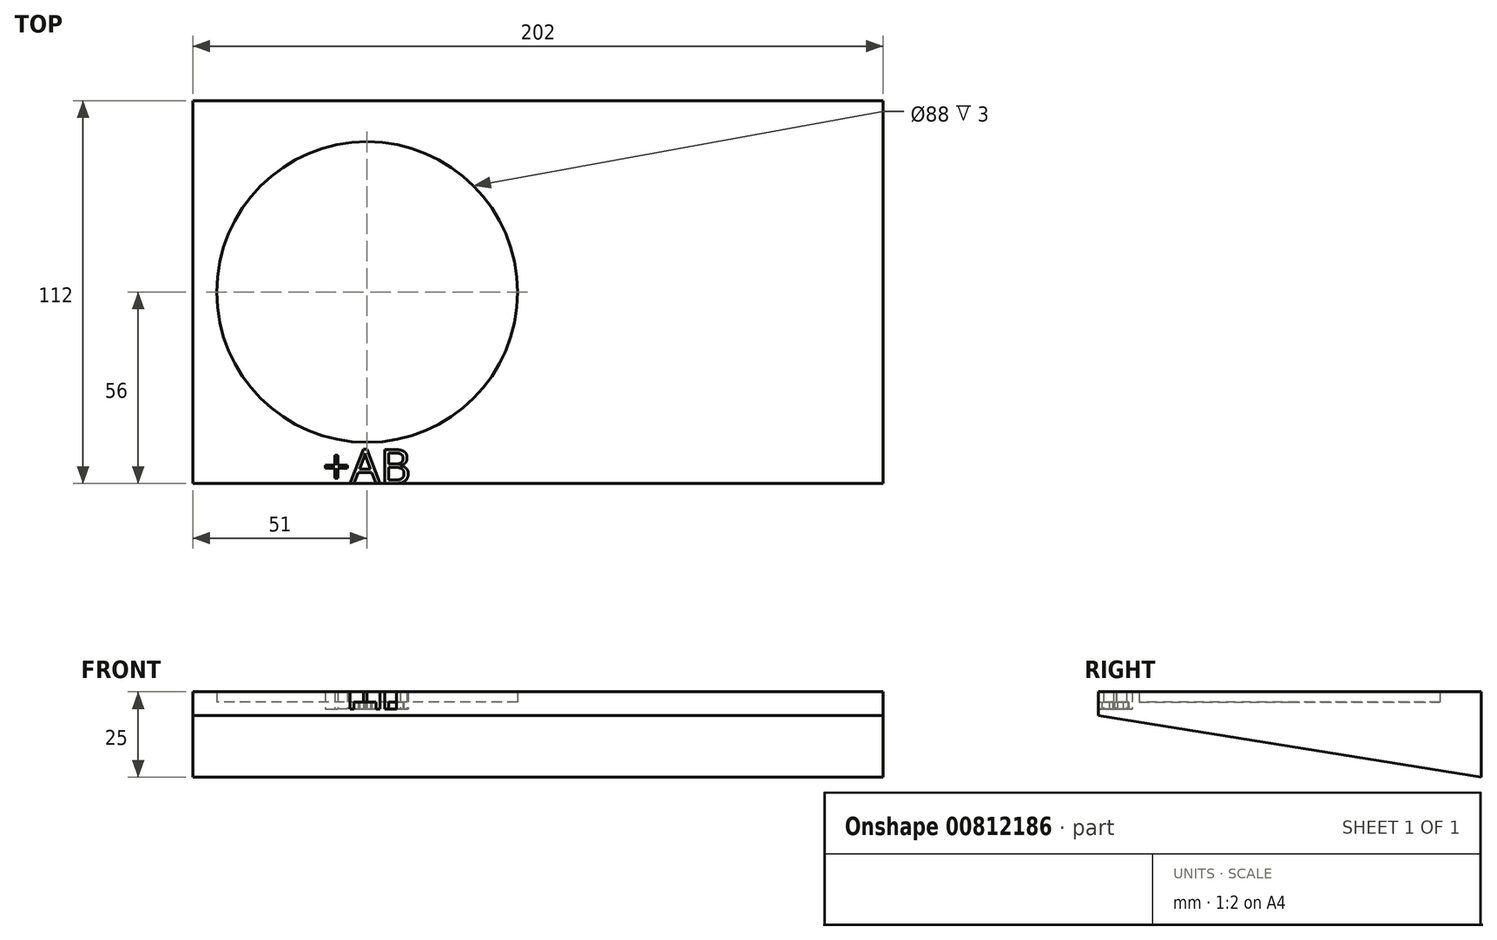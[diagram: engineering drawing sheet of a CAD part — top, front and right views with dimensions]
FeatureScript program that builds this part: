
annotation { "Feature Type Name" : "Feature", "Feature Type Description" : "" }
export const myFeature = defineFeature(function(context is Context, id is Id, definition is map)
    precondition{}
    {
        {
            var Q0;
            Q0=qCreatedBy(makeId("Top.planeOp"),FACE);
            var sketch = newSketch(context, id + "F0", { "sketchPlane" : qUnion([Q0])});
            skCircle(sketch, "E0", {"center": v(-50, 0) * mm, "radius": 46 * mm});
            skCircle(sketch, "E1", {"center": v(-50, 0) * mm, "radius": 44 * mm});
            skCircle(sketch, "E2.MirrorC", {"center": v(50, 0) * mm, "radius": 44 * mm});
            skCircle(sketch, "E3.MirrorC", {"center": v(50, 0) * mm, "radius": 46 * mm});
            skLineSegment(sketch, "E4.bottom", {"start": v(101, -56) * mm, "end": v(-101, -56) * mm});
            skLineSegment(sketch, "E4.top", {"start": v(101, 56) * mm, "end": v(-101, 56) * mm});
            skLineSegment(sketch, "E4.left", {"start": v(101, -56) * mm, "end": v(101, 56) * mm});
            skLineSegment(sketch, "E4.right", {"start": v(-101, -56) * mm, "end": v(-101, 56) * mm});
            skPoint(sketch, "E4.middle", {"position": v(0, 0) * mm});
            skText(sketch, "E5", { "text": "+AB", "fontName": "OpenSans-Regular.ttf"});
            skLineSegment(sketch, "E6", {"start": v(-50, 56) * mm, "end": v(-50, -56) * mm, "construction": true});
            skLineSegment(sketch, "E7", {"start": v(50, 56) * mm, "end": v(50, -56) * mm, "construction": true});
            const initialGuessF0  = {"E5": [-0.06293, -0.056, 1, 0, 0.01]};
            skSetInitialGuess(sketch, initialGuessF0);
            skSolve(sketch);
        }
        {
            var Q0;
            Q0=makeQuery(id+"F0.imprint","IMPRINT",FACE,{"disambiguationData":[TD([[makeQuery(id+"F0.imprint","IMPRINT",EDGE,{"derivedFrom":sQuery(id+"F0.wireOp",EDGE,"E0")}),-1.0]])]});
            var Q1;
            Q1=makeQuery(id+"F0.imprint","IMPRINT",FACE,{"disambiguationData":[TD([[makeQuery(id+"F0.imprint","IMPRINT",EDGE,{"derivedFrom":sQuery(id+"F0.wireOp",EDGE,"E0")}),1.0]])]});
            var Q2;
            Q2=makeQuery(id+"F0.imprint","IMPRINT",FACE,{"disambiguationData":[TD([[makeQuery(id+"F0.imprint","IMPRINT",EDGE,{"derivedFrom":sQuery(id+"F0.wireOp",EDGE,"E1")}),1.0]])]});
            var Q3;
            Q3=makeQuery(id+"F0.imprint","IMPRINT",FACE,{"disambiguationData":[TD([[makeQuery(id+"F0.imprint","IMPRINT",EDGE,{"derivedFrom":sQuery(id+"F0.wireOp",EDGE,"E2.MirrorC")}),-1.0]])]});
            var Q4;
            Q4=makeQuery(id+"F0.imprint","IMPRINT",FACE,{"disambiguationData":[TD([[makeQuery(id+"F0.imprint","IMPRINT",EDGE,{"derivedFrom":sQuery(id+"F0.wireOp",EDGE,"E2.MirrorC")}),1.0]])]});
            var Q5;
            Q5=makeQuery(id+"F0.imprint","IMPRINT",FACE,{"disambiguationData":[TD([[makeQuery(id+"F0.imprint","IMPRINT",EDGE,{"derivedFrom":sQuery(id+"F0.wireOp",EDGE,"E5.sketch_text.stroke-20")}),1.0]])]});
            var Q6;
            {var subQ0=sQuery(id+"F0.wireOp",EDGE,"E5.sketch_text.stroke-12");Q6=makeQuery(id+"F0.imprint","IMPRINT",FACE,{"disambiguationData":[TD([[makeQuery(id+"F0.imprint","IMPRINT",EDGE,{"derivedFrom":subQ0}),1.0]])]});}
            var Q7;
            Q7=makeQuery(id+"F0.imprint","IMPRINT",FACE,{"disambiguationData":[TD([[makeQuery(id+"F0.imprint","IMPRINT",EDGE,{"derivedFrom":sQuery(id+"F0.wireOp",EDGE,"E5.sketch_text.stroke-36")}),1.0]])]});
            var Q8;
            Q8=makeQuery(id+"F0.imprint","IMPRINT",FACE,{"disambiguationData":[TD([[makeQuery(id+"F0.imprint","IMPRINT",EDGE,{"derivedFrom":sQuery(id+"F0.wireOp",EDGE,"E5.sketch_text.stroke-43")}),1.0]])]});
            extrude(context, id + "F1", {"entities" : qUnion([Q0, Q1, Q2, Q3, Q4, Q5, Q6, Q7, Q8]), "depth" : 2 * mm, "offsetDistance" : 25 * mm});
        }
        {
            var Q0;
            Q0=makeQuery(id+"F1.opExtrude","CAP_FACE",FACE,{"disambiguationData":[OSD([sQuery(id+"F0.wireOp",EDGE,"E4.bottom"),sQuery(id+"F0.wireOp",EDGE,"E4.top"),sQuery(id+"F0.wireOp",EDGE,"E4.left"),sQuery(id+"F0.wireOp",EDGE,"E4.right"),sQuery(id+"F0.wireOp",EDGE,"E5.sketch_text.stroke-0"),sQuery(id+"F0.wireOp",EDGE,"E5.sketch_text.stroke-1"),sQuery(id+"F0.wireOp",EDGE,"E5.sketch_text.stroke-2"),sQuery(id+"F0.wireOp",EDGE,"E5.sketch_text.stroke-3"),sQuery(id+"F0.wireOp",EDGE,"E5.sketch_text.stroke-4"),sQuery(id+"F0.wireOp",EDGE,"E5.sketch_text.stroke-5"),sQuery(id+"F0.wireOp",EDGE,"E5.sketch_text.stroke-6"),sQuery(id+"F0.wireOp",EDGE,"E5.sketch_text.stroke-7"),sQuery(id+"F0.wireOp",EDGE,"E5.sketch_text.stroke-8"),sQuery(id+"F0.wireOp",EDGE,"E5.sketch_text.stroke-9"),sQuery(id+"F0.wireOp",EDGE,"E5.sketch_text.stroke-10"),sQuery(id+"F0.wireOp",EDGE,"E5.sketch_text.stroke-11"),sQuery(id+"F0.wireOp",EDGE,"E5.sketch_text.stroke-16"),sQuery(id+"F0.wireOp",EDGE,"E5.sketch_text.stroke-17"),sQuery(id+"F0.wireOp",EDGE,"E5.sketch_text.stroke-18"),sQuery(id+"F0.wireOp",EDGE,"E5.sketch_text.stroke-25"),sQuery(id+"F0.wireOp",EDGE,"E5.sketch_text.stroke-26"),sQuery(id+"F0.wireOp",EDGE,"E5.sketch_text.stroke-27"),sQuery(id+"F0.wireOp",EDGE,"E5.sketch_text.stroke-28"),sQuery(id+"F0.wireOp",EDGE,"E5.sketch_text.stroke-29"),sQuery(id+"F0.wireOp",EDGE,"E5.sketch_text.stroke-30"),sQuery(id+"F0.wireOp",EDGE,"E5.sketch_text.stroke-31"),sQuery(id+"F0.wireOp",EDGE,"E5.sketch_text.stroke-32"),sQuery(id+"F0.wireOp",EDGE,"E5.sketch_text.stroke-33"),sQuery(id+"F0.wireOp",EDGE,"E5.sketch_text.stroke-35")])],"isStart":false});
            var Q1;
            Q1 = qSketchRegion(id + "F0", true);
            var Q2;
            Q2=makeQuery(id+"F0.imprint","IMPRINT",FACE,{"disambiguationData":[TD([[makeQuery(id+"F0.imprint","IMPRINT",EDGE,{"derivedFrom":sQuery(id+"F0.wireOp",EDGE,"E5.sketch_text.stroke-20")}),1.0]])]});
            var Q3;
            Q3=makeQuery(id+"F0.imprint","IMPRINT",FACE,{"disambiguationData":[TD([[makeQuery(id+"F0.imprint","IMPRINT",EDGE,{"derivedFrom":sQuery(id+"F0.wireOp",EDGE,"E5.sketch_text.stroke-36")}),1.0]])]});
            var Q4;
            Q4=makeQuery(id+"F0.imprint","IMPRINT",FACE,{"disambiguationData":[TD([[makeQuery(id+"F0.imprint","IMPRINT",EDGE,{"derivedFrom":sQuery(id+"F0.wireOp",EDGE,"E5.sketch_text.stroke-43")}),1.0]])]});
            var Q5;
            Q5=makeQuery(id+"F0.imprint","IMPRINT",FACE,{"disambiguationData":[TD([[makeQuery(id+"F0.imprint","IMPRINT",EDGE,{"derivedFrom":sQuery(id+"F0.wireOp",EDGE,"E5.sketch_text.stroke-0")}),-1.0]])]});
            extrude(context, id + "F2", {"entities" : qUnion([Q0, Q1, Q2, Q3, Q4, Q5]), "operationType" : NewBodyOperationType.ADD, "oppositeDirection" : true, "depth" : 2 * mm, "offsetDistance" : 25 * mm});
        }
        {
            var Q0;
            Q0=makeQuery(id+"F0.imprint","IMPRINT",FACE,{"disambiguationData":[TD([[makeQuery(id+"F0.imprint","IMPRINT",EDGE,{"derivedFrom":sQuery(id+"F0.wireOp",EDGE,"E0")}),1.0]])]});
            var Q1;
            Q1=makeQuery(id+"F0.imprint","IMPRINT",FACE,{"disambiguationData":[TD([[makeQuery(id+"F0.imprint","IMPRINT",EDGE,{"derivedFrom":sQuery(id+"F0.wireOp",EDGE,"E2.MirrorC")}),1.0]])]});
            extrude(context, id + "F3", {"entities" : qUnion([Q0, Q1]), "operationType" : NewBodyOperationType.ADD, "depth" : 5 * mm, "offsetDistance" : 25 * mm});
        }
        {
            var Q0;
            {var subQ0=sQuery(id+"F0.wireOp",EDGE,"E5.sketch_text.stroke-18");var subQ1=sQuery(id+"F0.wireOp",EDGE,"E5.sketch_text.stroke-17");var subQ2=sQuery(id+"F0.wireOp",EDGE,"E5.sketch_text.stroke-16");var subQ3=sQuery(id+"F0.wireOp",EDGE,"E5.sketch_text.stroke-11");var subQ4=sQuery(id+"F0.wireOp",EDGE,"E5.sketch_text.stroke-10");var subQ5=sQuery(id+"F0.wireOp",EDGE,"E5.sketch_text.stroke-9");var subQ6=sQuery(id+"F0.wireOp",EDGE,"E5.sketch_text.stroke-8");var subQ7=sQuery(id+"F0.wireOp",EDGE,"E5.sketch_text.stroke-7");var subQ8=sQuery(id+"F0.wireOp",EDGE,"E5.sketch_text.stroke-6");var subQ9=sQuery(id+"F0.wireOp",EDGE,"E5.sketch_text.stroke-5");var subQ10=sQuery(id+"F0.wireOp",EDGE,"E5.sketch_text.stroke-4");var subQ11=sQuery(id+"F0.wireOp",EDGE,"E4.right");var subQ12=sQuery(id+"F0.wireOp",EDGE,"E4.bottom");var subQ16=sQuery(id+"F0.wireOp",EDGE,"E5.sketch_text.stroke-35");var subQ19=sQuery(id+"F0.wireOp",EDGE,"E4.top");var subQ20=sQuery(id+"F0.wireOp",EDGE,"E5.sketch_text.stroke-25");var subQ21=sQuery(id+"F0.wireOp",EDGE,"E4.left");var subQ22=sQuery(id+"F0.wireOp",EDGE,"E5.sketch_text.stroke-33");var subQ24=sQuery(id+"F0.wireOp",EDGE,"E5.sketch_text.stroke-3");var subQ25=sQuery(id+"F0.wireOp",EDGE,"E5.sketch_text.stroke-0");var subQ26=sQuery(id+"F0.wireOp",EDGE,"E5.sketch_text.stroke-1");var subQ27=sQuery(id+"F0.wireOp",EDGE,"E5.sketch_text.stroke-2");var subQ28=sQuery(id+"F0.wireOp",EDGE,"E5.sketch_text.stroke-26");var subQ29=sQuery(id+"F0.wireOp",EDGE,"E5.sketch_text.stroke-27");var subQ30=sQuery(id+"F0.wireOp",EDGE,"E5.sketch_text.stroke-28");var subQ31=sQuery(id+"F0.wireOp",EDGE,"E5.sketch_text.stroke-29");var subQ32=sQuery(id+"F0.wireOp",EDGE,"E5.sketch_text.stroke-30");var subQ33=sQuery(id+"F0.wireOp",EDGE,"E5.sketch_text.stroke-31");var subQ34=sQuery(id+"F0.wireOp",EDGE,"E5.sketch_text.stroke-32");Q0=makeQuery(id+"F6.boolean.opBoolean","MERGE",FACE,{"derivedFrom":[makeQuery(id+"F3.boolean.opBoolean","SPLIT",FACE,{"disambiguationData":[TD([makeQuery(id+"F1.opExtrude","SWEPT_FACE",FACE,{"disambiguationData":[OSD([subQ19])]})])],"derivedFrom":makeQuery(id+"F1.opExtrude","CAP_FACE",FACE,{"disambiguationData":[OSD([subQ12,subQ19,subQ21,subQ11,subQ25,subQ26,subQ27,subQ24,subQ10,subQ9,subQ8,subQ7,subQ6,subQ5,subQ4,subQ3,subQ2,subQ1,subQ0,subQ20,subQ28,subQ29,subQ30,subQ31,subQ32,subQ33,subQ34,subQ22,subQ16])],"isStart":false})}),makeQuery(id+"F6.opExtrude","SWEPT_FACE",FACE,{"disambiguationData":[OSD([sQuery(id+"F5.wireOp",EDGE,"E8.0")])]})]});}
            var Q1;
            Q1=makeQuery(id+"F3.opExtrude","CAP_FACE",FACE,{"disambiguationData":[OSD([sQuery(id+"F0.wireOp",EDGE,"E0"),sQuery(id+"F0.wireOp",EDGE,"E1")])],"isStart":false});
            extrude(context, id + "F4", {"entities" : qUnion([Q0]), "operationType" : NewBodyOperationType.ADD, "endBound" : BoundingType.UP_TO_SURFACE, "depth" : 25 * mm, "endBoundEntityFace" : qUnion([Q1]), "offsetDistance" : 25 * mm});
        }
        {
            var Q0;
            Q0=qCreatedBy(makeId("Right.planeOp"),FACE);
            var sketch = newSketch(context, id + "F5", { "sketchPlane" : qUnion([Q0])});
            skLineSegment(sketch, "E8.0", {"start": v(56, 0) * mm, "end": v(-56, 0) * mm});
            skLineSegment(sketch, "E9", {"start": v(56, 0) * mm, "end": v(56, -20) * mm});
            skLineSegment(sketch, "E10", {"start": v(-56, 0) * mm, "end": v(-56, -2) * mm});
            skLineSegment(sketch, "E11", {"start": v(-56, -2) * mm, "end": v(56, -20) * mm});
            skSolve(sketch);
        }
        {
            var Q0;
            Q0=makeQuery(id+"F5.imprint","IMPRINT",FACE,{"disambiguationData":[TD([[makeQuery(id+"F5.imprint","IMPRINT",EDGE,{"derivedFrom":sQuery(id+"F5.wireOp",EDGE,"E8.0")}),1.0]])]});
            var Q1;
            {var subQ0=sQuery(id+"F0.wireOp",EDGE,"E4.right");var subQ1=sQuery(id+"F0.wireOp",EDGE,"E4.bottom");Q1=makeQuery(id+"F2.opExtrude","CAP_VERTEX",VERTEX,{"disambiguationData":[OSD([subQ1,subQ0]),TDD([makeQuery(id+"F0.imprint","INTERSECT",VERTEX,{"derivedFrom":[subQ1,subQ0]})])],"isStart":false});}
            var Q2;
            {var subQ0=sQuery(id+"F0.wireOp",EDGE,"E4.left");var subQ1=sQuery(id+"F0.wireOp",EDGE,"E4.bottom");Q2=makeQuery(id+"F2.opExtrude","CAP_VERTEX",VERTEX,{"disambiguationData":[OSD([subQ1,subQ0]),TDD([makeQuery(id+"F0.imprint","INTERSECT",VERTEX,{"derivedFrom":[subQ1,subQ0]})])],"isStart":false});}
            extrude(context, id + "F6", {"entities" : qUnion([Q0]), "operationType" : NewBodyOperationType.ADD, "endBound" : BoundingType.UP_TO_VERTEX, "oppositeDirection" : true, "depth" : 25 * mm, "endBoundEntityVertex" : qUnion([Q1]), "offsetDistance" : 25 * mm, "hasSecondDirection" : true, "secondDirectionBound" : BoundingType.UP_TO_VERTEX, "secondDirectionOppositeDirection" : false, "secondDirectionDepth" : 25 * mm, "secondDirectionBoundEntityVertex" : qUnion([Q2])});
        }
    });
